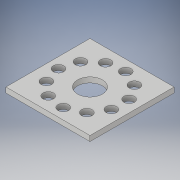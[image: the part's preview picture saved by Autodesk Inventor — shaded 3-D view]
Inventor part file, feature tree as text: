
AUTODESK INVENTOR PART (.ipt)
format: ipt  version: 2019 (Build 230136000, 136)  size: 134,656 bytes
history: native  units: in
note: dims shown in document units (in); Inventor stores cm internally (conversion verified against a paired STEP export)
features: extrude x2, sketch x2
ambient origin geometry x8: Origin, YZ Plane, XZ Plane, XY Plane, X Axis, Y Axis, Z Axis, Center Point
bodies: Solid1 (feature_tree)
feature tree (4):
  extrude  "Extrusion1"  Depth=0.25in
  extrude  "Extrusion2"  Depth=2.0in
  sketch  "Sketch1"  dims[d0=1.5in d1=0.25in]
  sketch  "Sketch2"  dims[d2=4.3307in d4=360.0deg d6=2.0in d7=2.0in d8=0.125in d9=0.0in d10=0.5906in d11=0.125in d12=0.0in]
